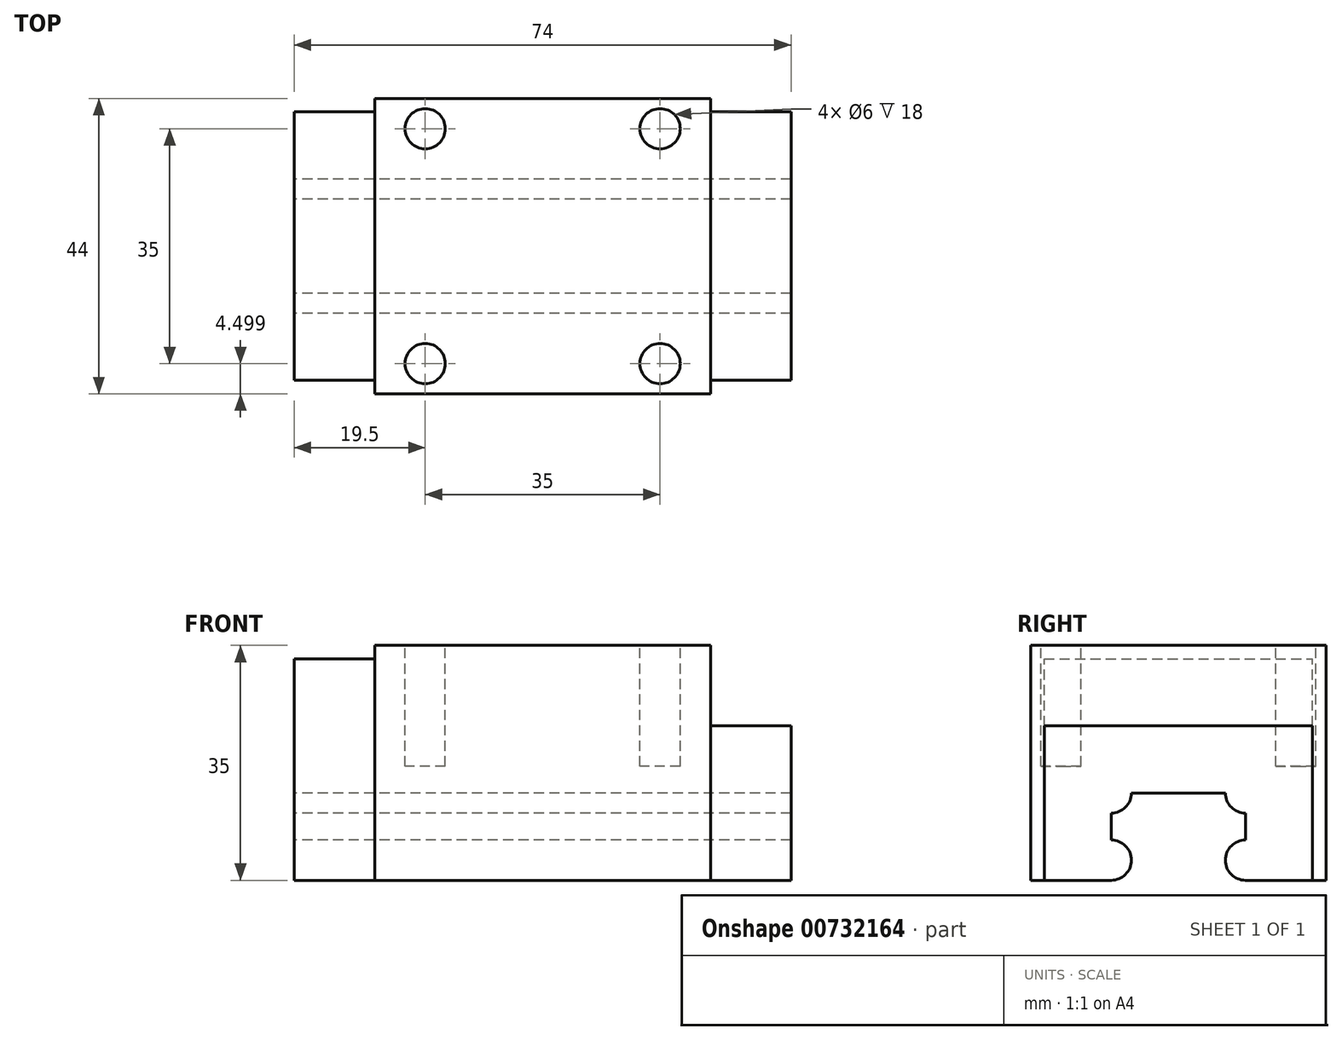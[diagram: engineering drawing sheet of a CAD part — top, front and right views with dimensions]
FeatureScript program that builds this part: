
annotation { "Feature Type Name" : "Feature", "Feature Type Description" : "" }
export const myFeature = defineFeature(function(context is Context, id is Id, definition is map)
    precondition{}
    {
        {
            var Q0;
            Q0=qCreatedBy(makeId("Right.planeOp"),FACE);
            var sketch = newSketch(context, id + "F0", { "sketchPlane" : qUnion([Q0])});
            skLineSegment(sketch, "E0", {"start": v(-26.04, 11) * mm, "end": v(-26.04, 15) * mm});
            skLineSegment(sketch, "E1", {"start": v(-23.04, 18) * mm, "end": v(-9.04, 18) * mm});
            skLineSegment(sketch, "E2", {"start": v(-6.04, 15) * mm, "end": v(-6.04, 11) * mm});
            skArc(sketch, "E3", {"start": v(-26.04, 5) * mm, "mid": v(-23.04, 8) * mm, "end": v(-26.04, 11) * mm});
            skArc(sketch, "E4", {"start": v(-6.04, 11) * mm, "mid": v(-9.04, 8) * mm, "end": v(-6.04, 5) * mm});
            skArc(sketch, "E5", {"start": v(-26.04, 15) * mm, "mid": v(-23.92, 15.88) * mm, "end": v(-23.04, 18) * mm});
            skArc(sketch, "E6", {"start": v(-9.04, 18) * mm, "mid": v(-8.16, 15.88) * mm, "end": v(-6.04, 15) * mm});
            skLineSegment(sketch, "E7", {"start": v(-38.04, 30) * mm, "end": v(5.96, 30) * mm});
            skLineSegment(sketch, "E8", {"start": v(-26.04, 5) * mm, "end": v(-38.04, 5) * mm});
            skLineSegment(sketch, "E9", {"start": v(-6.04, 5) * mm, "end": v(5.96, 5) * mm});
            skLineSegment(sketch, "E10", {"start": v(-38.04, 5) * mm, "end": v(-38.04, 30) * mm});
            skLineSegment(sketch, "E11", {"start": v(5.96, 5) * mm, "end": v(5.96, 30) * mm});
            skSolve(sketch);
        }
        {
            var Q0;
            Q0=qSketchRegion(id+"F0",true);
            extrude(context, id + "F1", {"entities" : qUnion([Q0]), "depth" : 74 * mm});
        }
        {
            var Q0;
            Q0=makeQuery(id+"F1.opExtrude","SWEPT_FACE",FACE,{"disambiguationData":[OSD([sQuery(id+"F0.wireOp",EDGE,"E7")])]});
            var sketch = newSketch(context, id + "F2", { "sketchPlane" : qUnion([Q0])});
            skLineSegment(sketch, "E12.bottom", {"start": v(74, -38.04) * mm, "end": v(62, -38.04) * mm});
            skLineSegment(sketch, "E12.top", {"start": v(74, 5.96) * mm, "end": v(62, 5.96) * mm});
            skLineSegment(sketch, "E12.left", {"start": v(74, -38.04) * mm, "end": v(74, 5.96) * mm});
            skLineSegment(sketch, "E12.right", {"start": v(62, -38.04) * mm, "end": v(62, 5.96) * mm});
            skLineSegment(sketch, "E13.bottom", {"start": v(0, -38.04) * mm, "end": v(12, -38.04) * mm});
            skLineSegment(sketch, "E13.top", {"start": v(0, 5.96) * mm, "end": v(12, 5.96) * mm});
            skLineSegment(sketch, "E13.left", {"start": v(0, -38.04) * mm, "end": v(0, 5.96) * mm});
            skLineSegment(sketch, "E13.right", {"start": v(12, -38.04) * mm, "end": v(12, 5.96) * mm});
            skSolve(sketch);
        }
        {
            var Q0;
            Q0=qSketchRegion(id+"F2",true);
            extrude(context, id + "F3", {"entities" : qUnion([Q0]), "operationType" : NewBodyOperationType.REMOVE, "oppositeDirection" : true, "depth" : 2 * mm});
        }
        {
            var Q0;
            Q0=makeQuery(id+"F1.opExtrude","SWEPT_FACE",FACE,{"disambiguationData":[OSD([sQuery(id+"F0.wireOp",EDGE,"E7")])]});
            var sketch = newSketch(context, id + "F4", { "sketchPlane" : qUnion([Q0])});
            skLineSegment(sketch, "E14.bottom", {"start": v(12, 5.96) * mm, "end": v(0, 5.96) * mm});
            skLineSegment(sketch, "E14.top", {"start": v(12, 3.96) * mm, "end": v(0, 3.96) * mm});
            skLineSegment(sketch, "E14.left", {"start": v(12, 5.96) * mm, "end": v(12, 3.96) * mm});
            skLineSegment(sketch, "E14.right", {"start": v(0, 5.96) * mm, "end": v(0, 3.96) * mm});
            skLineSegment(sketch, "E15.bottom", {"start": v(12, -38.04) * mm, "end": v(0, -38.04) * mm});
            skLineSegment(sketch, "E15.top", {"start": v(12, -36.04) * mm, "end": v(0, -36.04) * mm});
            skLineSegment(sketch, "E15.left", {"start": v(12, -38.04) * mm, "end": v(12, -36.04) * mm});
            skLineSegment(sketch, "E15.right", {"start": v(0, -38.04) * mm, "end": v(0, -36.04) * mm});
            skPoint(sketch, "E16.oppositeSnap0", {"position": v(6, -36.04) * mm});
            skLineSegment(sketch, "E16.bottom", {"start": v(62, -38.04) * mm, "end": v(74, -38.04) * mm});
            skLineSegment(sketch, "E16.top", {"start": v(62, -36.04) * mm, "end": v(74, -36.04) * mm});
            skLineSegment(sketch, "E16.left", {"start": v(62, -38.04) * mm, "end": v(62, -36.04) * mm});
            skLineSegment(sketch, "E16.right", {"start": v(74, -38.04) * mm, "end": v(74, -36.04) * mm});
            skLineSegment(sketch, "E17.bottom", {"start": v(62, 5.96) * mm, "end": v(74, 5.96) * mm});
            skLineSegment(sketch, "E17.top", {"start": v(62, 3.96) * mm, "end": v(74, 3.96) * mm});
            skLineSegment(sketch, "E17.left", {"start": v(62, 5.96) * mm, "end": v(62, 3.96) * mm});
            skLineSegment(sketch, "E17.right", {"start": v(74, 5.96) * mm, "end": v(74, 3.96) * mm});
            skSolve(sketch);
        }
        {
            var Q0;
            Q0=qSketchRegion(id+"F4",true);
            extrude(context, id + "F5", {"entities" : qUnion([Q0]), "operationType" : NewBodyOperationType.REMOVE, "oppositeDirection" : true, "depth" : 25 * mm});
        }
        {
            var Q0;
            Q0=makeQuery(id+"F1.opExtrude","SWEPT_FACE",FACE,{"disambiguationData":[OSD([sQuery(id+"F0.wireOp",EDGE,"E7")])]});
            var sketch = newSketch(context, id + "F6", { "sketchPlane" : qUnion([Q0])});
            skLineSegment(sketch, "E18.bottom", {"start": v(22.5, -33.54) * mm, "end": v(51.5, -33.54) * mm});
            skLineSegment(sketch, "E18.top", {"start": v(22.5, 1.46) * mm, "end": v(51.5, 1.46) * mm});
            skLineSegment(sketch, "E18.left", {"start": v(19.5, -30.54) * mm, "end": v(19.5, -1.54) * mm});
            skLineSegment(sketch, "E18.right", {"start": v(54.5, -30.54) * mm, "end": v(54.5, -1.54) * mm});
            skCircle(sketch, "E19", {"center": v(19.5, 1.46) * mm, "radius": 3 * mm});
            skCircle(sketch, "E20", {"center": v(54.5, 1.46) * mm, "radius": 3 * mm});
            skCircle(sketch, "E21", {"center": v(54.5, -33.54) * mm, "radius": 3 * mm});
            skCircle(sketch, "E22", {"center": v(19.5, -33.54) * mm, "radius": 3 * mm});
            skSolve(sketch);
        }
        {
            var Q0;
            {var subQ0=sQuery(id+"F6.wireOp",EDGE,"E19");var subQ1=makeQuery(id+"F6.imprint","INTERSECT",VERTEX,{"derivedFrom":[sQuery(id+"F6.wireOp",EDGE,"E18.top"),subQ0]});Q0=makeQuery(id+"F6.imprint","IMPRINT",FACE,{"disambiguationData":[TD([[makeQuery(id+"F6.imprint","IMPRINT",EDGE,{"disambiguationData":[TD([[subQ1,-1.0]])],"derivedFrom":subQ0}),1.0]])]});}
            var Q1;
            {var subQ0=sQuery(id+"F6.wireOp",EDGE,"E20");var subQ1=makeQuery(id+"F6.imprint","INTERSECT",VERTEX,{"derivedFrom":[sQuery(id+"F6.wireOp",EDGE,"E18.top"),subQ0]});Q1=makeQuery(id+"F6.imprint","IMPRINT",FACE,{"disambiguationData":[TD([[makeQuery(id+"F6.imprint","IMPRINT",EDGE,{"disambiguationData":[TD([[subQ1,-1.0]])],"derivedFrom":subQ0}),1.0]])]});}
            var Q2;
            {var subQ0=sQuery(id+"F6.wireOp",EDGE,"E21");var subQ1=makeQuery(id+"F6.imprint","INTERSECT",VERTEX,{"derivedFrom":[sQuery(id+"F6.wireOp",EDGE,"E18.bottom"),subQ0]});Q2=makeQuery(id+"F6.imprint","IMPRINT",FACE,{"disambiguationData":[TD([[makeQuery(id+"F6.imprint","IMPRINT",EDGE,{"disambiguationData":[TD([[subQ1,1.0]])],"derivedFrom":subQ0}),1.0]])]});}
            var Q3;
            {var subQ0=sQuery(id+"F6.wireOp",EDGE,"E22");var subQ1=makeQuery(id+"F6.imprint","INTERSECT",VERTEX,{"derivedFrom":[sQuery(id+"F6.wireOp",EDGE,"E18.bottom"),subQ0]});Q3=makeQuery(id+"F6.imprint","IMPRINT",FACE,{"disambiguationData":[TD([[makeQuery(id+"F6.imprint","IMPRINT",EDGE,{"disambiguationData":[TD([[subQ1,-1.0]])],"derivedFrom":subQ0}),1.0]])]});}
            extrude(context, id + "F7", {"entities" : qUnion([Q0, Q1, Q2, Q3]), "operationType" : NewBodyOperationType.REMOVE, "oppositeDirection" : true, "depth" : 8 * mm});
        }
        {
            var Q0;
            Q0=makeQuery(id+"F1.opExtrude","SWEPT_FACE",FACE,{"disambiguationData":[OSD([sQuery(id+"F0.wireOp",EDGE,"E7")])]});
            var sketch = newSketch(context, id + "F8", { "sketchPlane" : qUnion([Q0])});
            skLineSegment(sketch, "E23.bottom", {"start": v(12, -38.04) * mm, "end": v(62, -38.04) * mm});
            skLineSegment(sketch, "E23.top", {"start": v(12, 5.96) * mm, "end": v(62, 5.96) * mm});
            skLineSegment(sketch, "E23.left", {"start": v(12, -38.04) * mm, "end": v(12, 5.96) * mm});
            skLineSegment(sketch, "E23.right", {"start": v(62, -38.04) * mm, "end": v(62, 5.96) * mm});
            skCircle(sketch, "E24", {"center": v(19.5, 1.46) * mm, "radius": 3 * mm});
            skCircle(sketch, "E25", {"center": v(54.5, 1.46) * mm, "radius": 3 * mm});
            skCircle(sketch, "E26", {"center": v(54.5, -33.54) * mm, "radius": 3 * mm});
            skCircle(sketch, "E27", {"center": v(19.5, -33.54) * mm, "radius": 3 * mm});
            skSolve(sketch);
        }
        {
            var Q0;
            Q0=makeQuery(id+"F8.imprint","IMPRINT",FACE,{"disambiguationData":[TD([[makeQuery(id+"F8.imprint","IMPRINT",EDGE,{"derivedFrom":sQuery(id+"F8.wireOp",EDGE,"E23.bottom")}),-1.0]])]});
            extrude(context, id + "F9", {"entities" : qUnion([Q0]), "operationType" : NewBodyOperationType.ADD, "depth" : 10 * mm});
        }
        {
            var Q0;
            Q0=makeQuery(id+"F3.boolean.opBoolean","COPY",FACE,{"derivedFrom":makeQuery(id+"F3.opExtrude","CAP_FACE",FACE,{"disambiguationData":[OSD([sQuery(id+"F2.wireOp",EDGE,"E13.bottom"),sQuery(id+"F2.wireOp",EDGE,"E13.top"),sQuery(id+"F2.wireOp",EDGE,"E13.left"),sQuery(id+"F2.wireOp",EDGE,"E13.right")])],"isStart":false})});
            var sketch = newSketch(context, id + "F10", { "sketchPlane" : qUnion([Q0])});
            skLineSegment(sketch, "E28.bottom", {"start": v(0, -36.04) * mm, "end": v(12, -36.04) * mm});
            skLineSegment(sketch, "E28.top", {"start": v(0, 3.96) * mm, "end": v(12, 3.96) * mm});
            skLineSegment(sketch, "E28.left", {"start": v(0, -36.04) * mm, "end": v(0, 3.96) * mm});
            skLineSegment(sketch, "E28.right", {"start": v(12, -36.04) * mm, "end": v(12, 3.96) * mm});
            skLineSegment(sketch, "E29.bottom", {"start": v(12, -36.04) * mm, "end": v(74, -36.04) * mm});
            skLineSegment(sketch, "E29.top", {"start": v(12, 3.96) * mm, "end": v(74, 3.96) * mm});
            skLineSegment(sketch, "E29.right", {"start": v(74, -36.04) * mm, "end": v(74, 3.96) * mm});
            skLineSegment(sketch, "E30.bottom", {"start": v(74, -36.04) * mm, "end": v(62, -36.04) * mm});
            skLineSegment(sketch, "E30.top", {"start": v(74, 3.96) * mm, "end": v(62, 3.96) * mm});
            skLineSegment(sketch, "E30.right", {"start": v(62, -36.04) * mm, "end": v(62, 3.96) * mm});
            skSolve(sketch);
        }
        {
            var Q0;
            Q0=makeQuery(id+"F10.imprint","IMPRINT",FACE,{"disambiguationData":[TD([[makeQuery(id+"F10.imprint","IMPRINT",EDGE,{"derivedFrom":sQuery(id+"F10.wireOp",EDGE,"E28.bottom")}),-1.0]])]});
            var Q1;
            Q1=makeQuery(id+"F10.imprint","IMPRINT",FACE,{"disambiguationData":[TD([[makeQuery(id+"F10.imprint","IMPRINT",EDGE,{"derivedFrom":sQuery(id+"F10.wireOp",EDGE,"E30.bottom")}),-1.0]])]});
            extrude(context, id + "F11", {"entities" : qUnion([Q0, Q1]), "operationType" : NewBodyOperationType.ADD, "depth" : 10 * mm});
        }
    });
